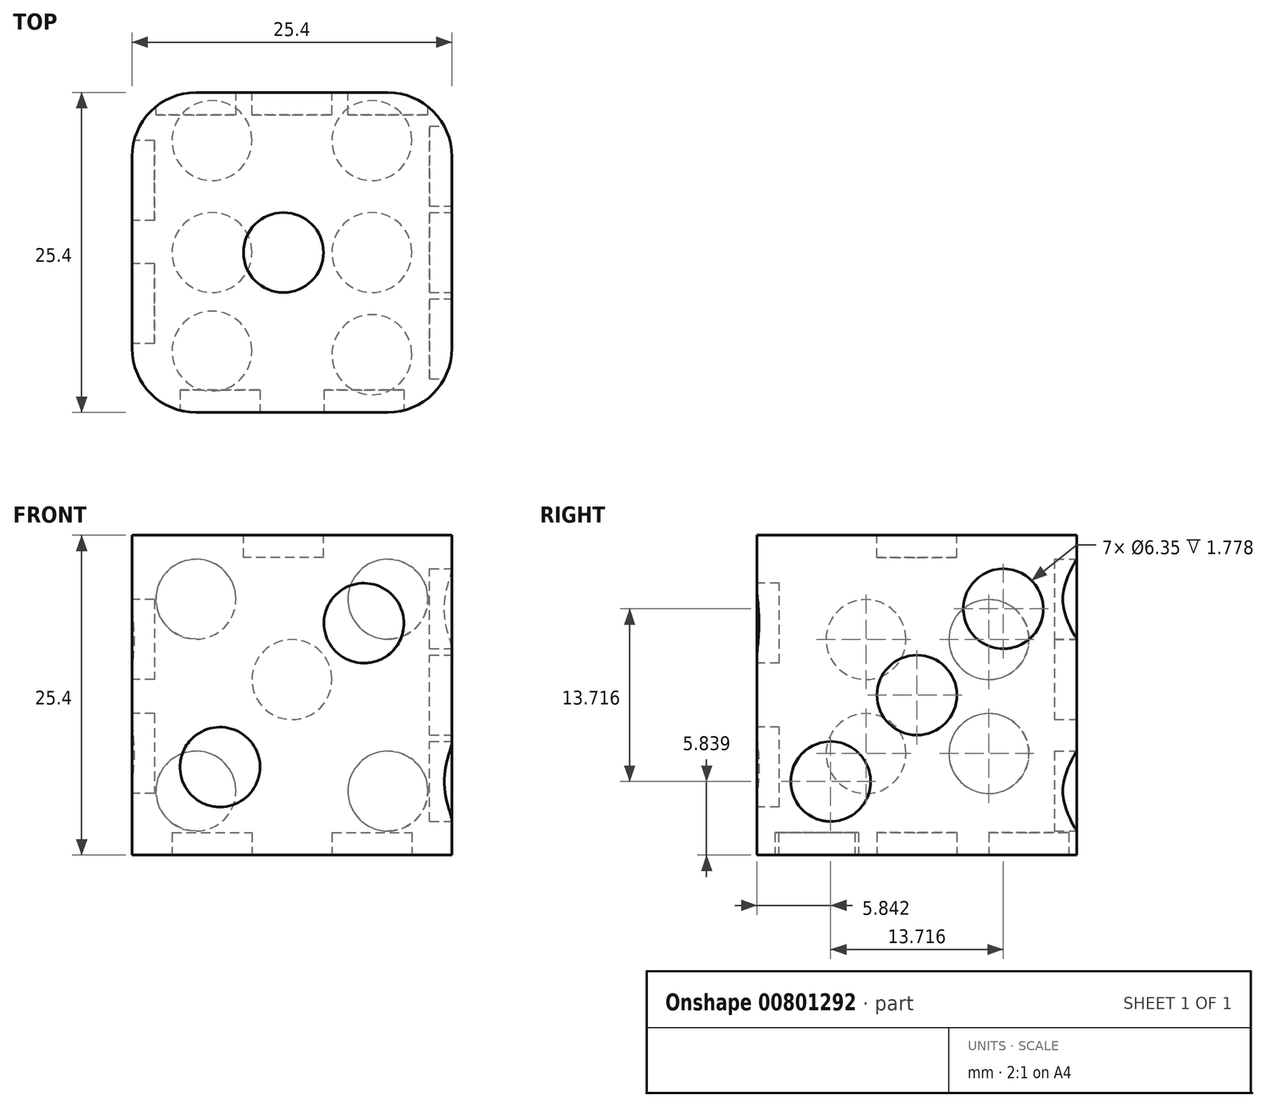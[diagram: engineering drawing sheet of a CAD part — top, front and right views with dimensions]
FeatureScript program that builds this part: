
annotation { "Feature Type Name" : "Feature", "Feature Type Description" : "" }
export const myFeature = defineFeature(function(context is Context, id is Id, definition is map)
    precondition{}
    {
        {
            var Q0;
            Q0=qCreatedBy(makeId("Front.planeOp"),FACE);
            var sketch = newSketch(context, id + "F0", { "sketchPlane" : qUnion([Q0])});
            skLineSegment(sketch, "E0.bottom", {"start": v(-38.66, 31.35) * mm, "end": v(-13.26, 31.35) * mm});
            skLineSegment(sketch, "E0.top", {"start": v(-38.66, 5.95) * mm, "end": v(-13.26, 5.95) * mm});
            skLineSegment(sketch, "E0.left", {"start": v(-38.66, 31.35) * mm, "end": v(-38.66, 5.95) * mm});
            skLineSegment(sketch, "E0.right", {"start": v(-13.26, 31.35) * mm, "end": v(-13.26, 5.95) * mm});
            skSolve(sketch);
        }
        {
            var Q0;
            Q0=makeQuery(id+"F0.imprint","IMPRINT",FACE,{"disambiguationData":[TD([[makeQuery(id+"F0.imprint","IMPRINT",EDGE,{"derivedFrom":sQuery(id+"F0.wireOp",EDGE,"E0.bottom")}),-1.0]])]});
            extrude(context, id + "F1", {"entities" : qUnion([Q0]), "depth" : 25.4 * mm, "offsetDistance" : 25.4 * mm});
        }
        {
            var Q0;
            Q0=makeQuery(id+"F1.opExtrude","CAP_FACE",FACE,{"disambiguationData":[OSD([sQuery(id+"F0.wireOp",EDGE,"E0.bottom"),sQuery(id+"F0.wireOp",EDGE,"E0.top"),sQuery(id+"F0.wireOp",EDGE,"E0.left"),sQuery(id+"F0.wireOp",EDGE,"E0.right")])],"isStart":false});
            var sketch = newSketch(context, id + "F2", { "sketchPlane" : qUnion([Q0])});
            skCircle(sketch, "E1", {"center": v(-31.67, 12.93) * mm, "radius": 3.18 * mm});
            skSolve(sketch);
        }
        {
            var Q0;
            Q0=makeQuery(id+"F1.opExtrude","CAP_FACE",FACE,{"disambiguationData":[OSD([sQuery(id+"F0.wireOp",EDGE,"E0.bottom"),sQuery(id+"F0.wireOp",EDGE,"E0.top"),sQuery(id+"F0.wireOp",EDGE,"E0.left"),sQuery(id+"F0.wireOp",EDGE,"E0.right")])],"isStart":false});
            var sketch = newSketch(context, id + "F3", { "sketchPlane" : qUnion([Q0])});
            skCircle(sketch, "E2", {"center": v(-20.24, 24.36) * mm, "radius": 3.18 * mm});
            skSolve(sketch);
        }
        {
            var Q0;
            Q0=makeQuery(id+"F1.opExtrude","SWEPT_FACE",FACE,{"disambiguationData":[OSD([sQuery(id+"F0.wireOp",EDGE,"E0.bottom")])]});
            var sketch = newSketch(context, id + "F4", { "sketchPlane" : qUnion([Q0])});
            skCircle(sketch, "E3", {"center": v(-26.63, -12.7) * mm, "radius": 3.18 * mm});
            skPoint(sketch, "E3.centerSnap0", {"position": v(-38.66, -12.7) * mm});
            skSolve(sketch);
        }
        {
            var Q0;
            Q0=makeQuery(id+"F1.opExtrude","SWEPT_FACE",FACE,{"disambiguationData":[OSD([sQuery(id+"F0.wireOp",EDGE,"E0.left")])]});
            var sketch = newSketch(context, id + "F5", { "sketchPlane" : qUnion([Q0])});
            skCircle(sketch, "E4", {"center": v(16.75, 23.06) * mm, "radius": 3.18 * mm});
            skCircle(sketch, "E5", {"center": v(16.75, 14) * mm, "radius": 3.18 * mm});
            skCircle(sketch, "E6", {"center": v(6.99, 23.06) * mm, "radius": 3.18 * mm});
            skCircle(sketch, "E7", {"center": v(6.99, 14) * mm, "radius": 3.18 * mm});
            skSolve(sketch);
        }
        {
            var Q0;
            Q0=makeQuery(id+"F1.opExtrude","SWEPT_FACE",FACE,{"disambiguationData":[OSD([sQuery(id+"F0.wireOp",EDGE,"E0.right")])]});
            var sketch = newSketch(context, id + "F6", { "sketchPlane" : qUnion([Q0])});
            skCircle(sketch, "E8", {"center": v(-12.7, 18.65) * mm, "radius": 3.18 * mm});
            skPoint(sketch, "E8.centerSnap0", {"position": v(-12.7, 5.95) * mm});
            skCircle(sketch, "E9", {"center": v(-19.56, 11.79) * mm, "radius": 3.18 * mm});
            skCircle(sketch, "E10", {"center": v(-5.84, 25.5) * mm, "radius": 3.18 * mm});
            skSolve(sketch);
        }
        {
            var Q0;
            Q0=makeQuery(id+"F1.opExtrude","SWEPT_FACE",FACE,{"disambiguationData":[OSD([sQuery(id+"F0.wireOp",EDGE,"E0.top")])]});
            var sketch = newSketch(context, id + "F7", { "sketchPlane" : qUnion([Q0])});
            skCircle(sketch, "E11", {"center": v(-32.3, 12.7) * mm, "radius": 3.18 * mm});
            skCircle(sketch, "E12", {"center": v(-19.6, 12.7) * mm, "radius": 3.18 * mm});
            skCircle(sketch, "E13", {"center": v(-32.3, 20.53) * mm, "radius": 3.18 * mm});
            skCircle(sketch, "E14", {"center": v(-32.3, 3.81) * mm, "radius": 3.18 * mm});
            skCircle(sketch, "E15", {"center": v(-19.6, 3.81) * mm, "radius": 3.18 * mm});
            skCircle(sketch, "E16", {"center": v(-19.6, 20.81) * mm, "radius": 3.18 * mm});
            skSolve(sketch);
        }
        {
            var Q0;
            Q0=makeQuery(id+"F1.opExtrude","CAP_FACE",FACE,{"disambiguationData":[OSD([sQuery(id+"F0.wireOp",EDGE,"E0.bottom"),sQuery(id+"F0.wireOp",EDGE,"E0.top"),sQuery(id+"F0.wireOp",EDGE,"E0.left"),sQuery(id+"F0.wireOp",EDGE,"E0.right")])],"isStart":true});
            var sketch = newSketch(context, id + "F8", { "sketchPlane" : qUnion([Q0])});
            skCircle(sketch, "E17", {"center": v(25.96, 19.88) * mm, "radius": 3.18 * mm});
            skCircle(sketch, "E18", {"center": v(18.34, 26.27) * mm, "radius": 3.18 * mm});
            skCircle(sketch, "E19", {"center": v(18.34, 11.03) * mm, "radius": 3.18 * mm});
            skCircle(sketch, "E20", {"center": v(33.58, 11.03) * mm, "radius": 3.18 * mm});
            skCircle(sketch, "E21", {"center": v(33.58, 26.27) * mm, "radius": 3.18 * mm});
            skSolve(sketch);
        }
        {
            var Q0;
            Q0 = qSketchRegion(id + "F2", true);
            extrude(context, id + "F9", {"entities" : qUnion([Q0]), "operationType" : NewBodyOperationType.REMOVE, "oppositeDirection" : true, "depth" : 1.78 * mm, "offsetDistance" : 25.4 * mm});
        }
        {
            var Q0;
            Q0 = qSketchRegion(id + "F3", true);
            extrude(context, id + "F10", {"entities" : qUnion([Q0]), "operationType" : NewBodyOperationType.REMOVE, "oppositeDirection" : true, "depth" : 1.78 * mm, "offsetDistance" : 25.4 * mm});
        }
        {
            var Q0;
            Q0 = qSketchRegion(id + "F4", true);
            extrude(context, id + "F11", {"entities" : qUnion([Q0]), "operationType" : NewBodyOperationType.REMOVE, "oppositeDirection" : true, "depth" : 1.78 * mm, "offsetDistance" : 25.4 * mm});
        }
        {
            var Q0;
            Q0 = qSketchRegion(id + "F5", true);
            extrude(context, id + "F12", {"entities" : qUnion([Q0]), "operationType" : NewBodyOperationType.REMOVE, "oppositeDirection" : true, "depth" : 1.78 * mm, "offsetDistance" : 25.4 * mm});
        }
        {
            var Q0;
            Q0 = qSketchRegion(id + "F6", true);
            extrude(context, id + "F13", {"entities" : qUnion([Q0]), "operationType" : NewBodyOperationType.REMOVE, "oppositeDirection" : true, "depth" : 1.78 * mm, "offsetDistance" : 25.4 * mm});
        }
        {
            var Q0;
            Q0 = qSketchRegion(id + "F7", true);
            extrude(context, id + "F14", {"entities" : qUnion([Q0]), "operationType" : NewBodyOperationType.REMOVE, "oppositeDirection" : true, "depth" : 1.78 * mm, "offsetDistance" : 25.4 * mm});
        }
        {
            var Q0;
            Q0 = qSketchRegion(id + "F8", true);
            extrude(context, id + "F15", {"entities" : qUnion([Q0]), "operationType" : NewBodyOperationType.REMOVE, "oppositeDirection" : true, "depth" : 1.78 * mm, "offsetDistance" : 25.4 * mm});
        }
        {
            var Q0;
            Q0=makeQuery(id+"F1.opExtrude","CAP_EDGE",EDGE,{"disambiguationData":[OSD([sQuery(id+"F0.wireOp",EDGE,"E0.left")])],"isStart":false});
            var Q1;
            Q1=makeQuery(id+"F1.opExtrude","CAP_EDGE",EDGE,{"disambiguationData":[OSD([sQuery(id+"F0.wireOp",EDGE,"E0.right")])],"isStart":false});
            var Q2;
            Q2=makeQuery(id+"F1.opExtrude","CAP_EDGE",EDGE,{"disambiguationData":[OSD([sQuery(id+"F0.wireOp",EDGE,"E0.right")])],"isStart":true});
            var Q3;
            Q3=makeQuery(id+"F1.opExtrude","CAP_EDGE",EDGE,{"disambiguationData":[OSD([sQuery(id+"F0.wireOp",EDGE,"E0.left")])],"isStart":true});
            fillet(context, id + "F16", {"entities" : qUnion([Q0, Q1, Q2, Q3]), "radius" : 5.08 * mm, "tangentPropagation" : true, "allowEdgeOverflow" : false});
        }
    });
